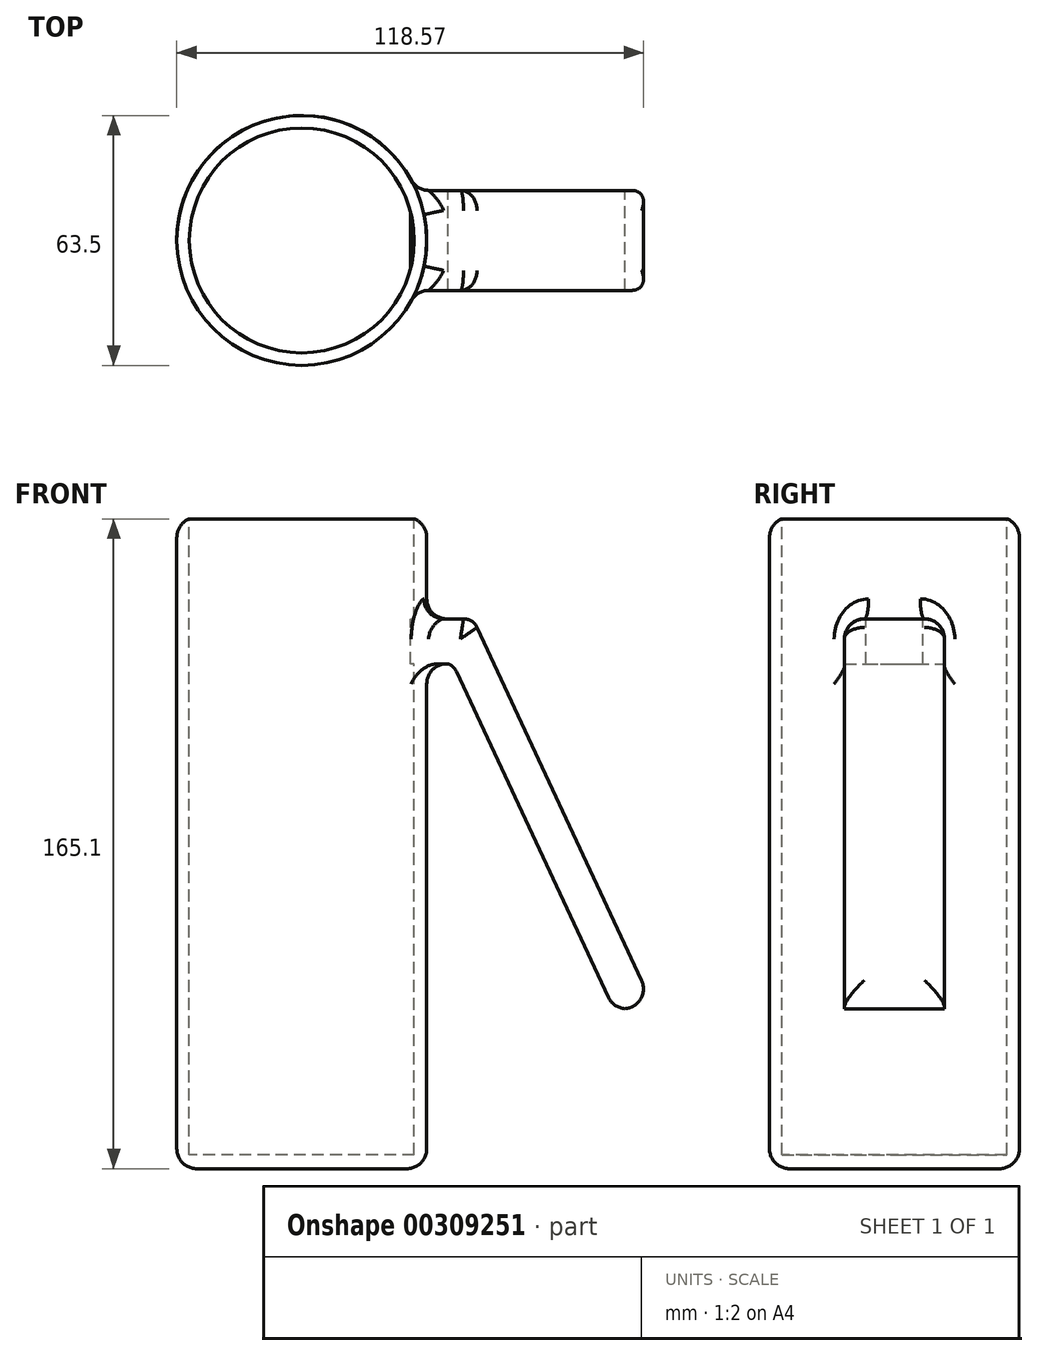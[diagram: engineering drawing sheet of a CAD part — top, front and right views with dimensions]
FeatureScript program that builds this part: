
annotation { "Feature Type Name" : "Feature", "Feature Type Description" : "" }
export const myFeature = defineFeature(function(context is Context, id is Id, definition is map)
    precondition{}
    {
        {
            var Q0;
            Q0=qCreatedBy(makeId("Front.planeOp"),FACE);
            var sketch = newSketch(context, id + "F0", { "sketchPlane" : qUnion([Q0])});
            skLineSegment(sketch, "E0", {"start": v(-67.54, 76.05) * mm, "end": v(-4.04, 76.05) * mm});
            skLineSegment(sketch, "E1", {"start": v(-4.04, 76.05) * mm, "end": v(-4.04, 50.65) * mm});
            skLineSegment(sketch, "E2", {"start": v(-67.54, 76.05) * mm, "end": v(-67.54, -89.05) * mm});
            skLineSegment(sketch, "E3", {"start": v(-67.54, -89.05) * mm, "end": v(-4.04, -89.05) * mm});
            skLineSegment(sketch, "E4", {"start": v(-4.04, -89.05) * mm, "end": v(-4.04, 39.22) * mm});
            skLineSegment(sketch, "E5", {"start": v(-35.8, 76.05) * mm, "end": v(-35.8, -89.05) * mm});
            skLineSegment(sketch, "E6", {"start": v(-4.04, 39.22) * mm, "end": v(-4.04, 50.65) * mm});
            skSolve(sketch);
        }
        {
            var Q0;
            {var subQ0=sQuery(id+"F0.wireOp",EDGE,"E2");Q0=makeQuery(id+"F0.imprint","IMPRINT",FACE,{"disambiguationData":[TD([[makeQuery(id+"F0.imprint","IMPRINT",EDGE,{"derivedFrom":subQ0}),1.0]])]});}
            var Q1;
            Q1=sQuery(id+"F0.wireOp",EDGE,"E5");
            revolve(context, id + "F1", {"entities" : qUnion([Q0]), "axis" : qUnion([Q1]), "revolveType" : RevolveType.FULL});
        }
        {
            var Q0;
            Q0=makeQuery(id+"F1.opRevolve","SWEPT_FACE",FACE,{"disambiguationData":[OSD([sQuery(id+"F0.wireOp",EDGE,"E0")])]});
            var sketch = newSketch(context, id + "F2", { "sketchPlane" : qUnion([Q0])});
            skCircle(sketch, "E7", {"center": v(-35.8, 0) * mm, "radius": 28.58 * mm});
            skSolve(sketch);
        }
        {
            var Q0;
            Q0=makeQuery(id+"F2.imprint","IMPRINT",FACE,{"disambiguationData":[TD([[makeQuery(id+"F2.imprint","IMPRINT",EDGE,{"derivedFrom":sQuery(id+"F2.wireOp",EDGE,"E7")}),1.0]])]});
            extrude(context, id + "F3", {"entities" : qUnion([Q0]), "operationType" : NewBodyOperationType.REMOVE, "endBound" : BoundingType.SYMMETRIC, "oppositeDirection" : true, "depth" : 323.09 * mm});
        }
        {
            var Q0;
            Q0=qCreatedBy(makeId("Front.planeOp"),FACE);
            var sketch = newSketch(context, id + "F4", { "sketchPlane" : qUnion([Q0])});
            skLineSegment(sketch, "E8", {"start": v(-8.14, 75.83) * mm, "end": v(-8.14, -82.77) * mm});
            skLineSegment(sketch, "E9", {"start": v(-8.14, 50.65) * mm, "end": v(5.3, 50.65) * mm});
            skLineSegment(sketch, "E10", {"start": v(-8.14, 39.22) * mm, "end": v(1.39, 39.22) * mm});
            skLineSegment(sketch, "E11", {"start": v(3.5, 37.26) * mm, "end": v(43.45, -48.41) * mm});
            skLineSegment(sketch, "E12", {"start": v(43.45, -48.41) * mm, "end": v(53.92, -48.41) * mm});
            skLineSegment(sketch, "E13", {"start": v(53.92, -48.41) * mm, "end": v(8.76, 48.45) * mm});
            skPoint(sketch, "E14.visualSharp", {"position": v(7.73, 50.65) * mm});
            skArc(sketch, "E14.filletArc", {"start": v(8.76, 48.45) * mm, "mid": v(7.35, 50.05) * mm, "end": v(5.3, 50.65) * mm});
            skPoint(sketch, "E15.visualSharp", {"position": v(2.6, 39.22) * mm});
            skArc(sketch, "E15.filletArc", {"start": v(3.5, 37.26) * mm, "mid": v(2.64, 38.45) * mm, "end": v(1.39, 39.22) * mm});
            skSolve(sketch);
        }
        {
            var Q0;
            {var subQ1=sQuery(id+"F4.wireOp",EDGE,"E9");Q0=makeQuery(id+"F4.imprint","IMPRINT",FACE,{"disambiguationData":[TD([[makeQuery(id+"F4.imprint","IMPRINT",EDGE,{"derivedFrom":subQ1}),-1.0]])]});}
            extrude(context, id + "F5", {"entities" : qUnion([Q0]), "operationType" : NewBodyOperationType.ADD, "endBound" : BoundingType.SYMMETRIC, "depth" : 25.4 * mm});
        }
        {
            var Q0;
            Q0=makeQuery(id+"F1.opRevolve","SWEPT_FACE",FACE,{"disambiguationData":[OSD([sQuery(id+"F0.wireOp",EDGE,"E2")])]});
            var Q1;
            Q1=makeQuery(id+"F5.opExtrude","CAP_EDGE",EDGE,{"disambiguationData":[OSD([sQuery(id+"F4.wireOp",EDGE,"E9")])],"isStart":false});
            var Q2;
            Q2=makeQuery(id+"F5.opExtrude","SWEPT_EDGE",EDGE,{"disambiguationData":[OSD([sQuery(id+"F4.wireOp",EDGE,"E13"),sQuery(id+"F4.wireOp",EDGE,"E14.filletArc")])]});
            var Q3;
            Q3=makeQuery(id+"F5.opExtrude","CAP_EDGE",EDGE,{"disambiguationData":[OSD([sQuery(id+"F4.wireOp",EDGE,"E13")])],"isStart":true});
            var Q4;
            Q4=makeQuery(id+"F5.opExtrude","SWEPT_EDGE",EDGE,{"disambiguationData":[OSD([sQuery(id+"F4.wireOp",EDGE,"E11"),sQuery(id+"F4.wireOp",EDGE,"E12")])]});
            var Q5;
            Q5=makeQuery(id+"F5.opExtrude","SWEPT_EDGE",EDGE,{"disambiguationData":[OSD([sQuery(id+"F4.wireOp",EDGE,"E12"),sQuery(id+"F4.wireOp",EDGE,"E13")])]});
            fillet(context, id + "F6", {"entities" : qUnion([Q0, Q1, Q2, Q3, Q4, Q5]), "radius" : 5.08 * mm, "tangentPropagation" : true, "allowEdgeOverflow" : false});
        }
    });
